# Revit family: Geberit pisuvar Preda, entegre deşarj kontrollü, elektrikli_PRO_224443
name_source: partatom
category: Plumbing Fixtures
revit_build: Autodesk Revit 2018 (Build: 20190510_1515(x64)
units: mm (PartAtom-declared; Revit-internal decimal feet)

## family parameters
Always vertical = Yes
Cut with Voids When Loaded = No
OmniClass Number = 23.45.05.21
OmniClass Title = Plumbing Fixtures - Sanitary Disposal Units
Part Type = Normal
Room Calculation Point = Yes
Round Connector Dimension = Use Diameter
Shared = No
Work Plane-Based = No

## types (1)
- 116.072.00.1 Geberit pisuvar Preda, entegre deşarj kontrollü, elektrikli
    116072_0_view = Yes
    Application purposes = Otomatik, su tasarrufu sağlayan deşarj ile kullanım için
Entegre kumandalı veya entegre kumandaya yönelik pisuvarlarda Geberit montaj elemanları için
    Application range = Plumbing fixture
    Article number key = 116.072.00.1
    BIM Content Version = GEB MG 1.2
    BIM Content revision date = 2020.05.18
    Bekleme modunda güç tüketimi = < 0.1 W
    Brand = Geberit
    CW Connection = Yes
    Characteristics = Bacak algılamalı IR kullanıcı algılaması
Kanalsız
Pisuvar deşarj kontrolü seramik çıkarılmadan önden değiştirilebilir
Püskürtme başlığı, seramik çıkarılmadan önden değiştirilebilir
Sifon, seramik çıkarılmadan yukarıdan değiştirilebilir
Sifon bağlantısının yüksekliği takımsız olarak ayarlanabilir
Drenaj sistemi seramik çıkarılmadan temizlenebilir
Su tasarrufu sağlayan hibrit modu ayarlanabilir
Anti-vandal
Ön deşarj ayarlanabilir
Güç kesintisi kontrolü
Elektrik kesildiğinde valf kapatma fonksiyonu
Geberit servis kumandası ile fonksiyonlar ayarlanabilir ve sorgulanabilir
Yıkama miktarı, deşarj süresi üzerinden deşarj başına 0,5 litreye kadar azaltılabilir
Pisuvar seramiği için deşarj başına 0,5 litre deşarj suyu garanti edilir, EN 13407 uyarınca
DIN 4109 uyarınca batarya grubu II
    Description = Geberit pisuvar Preda, entegre deşarj kontrollü, elektrikli
    EAN code basic data = 4025416529828
    GEB_culture = tr-TR
    GEB_generic_description = Bathroom collection
    GEB_generic_manufacturer = generic
    GEB_pimversion = 22.02.12
    GEB_processing_type = T
    GEB_reference = PRO_224443
    GEB_translations = {"ATT_10673":"EAN code basic data","ATT_10773":"Çalışma basıncı","ATT_10847":"Hesaplanan akış hızı için minimum akış basıncı","ATT_459792":"Renk / Yüzey","ATT_10851":"Nominal şebeke gerilimi","ATT_10853":"Şebeke frekansı","ATT_10817":"Güç tüketimi","ATT_156863":"Bekleme modunda güç tüketimi","applicationPurposes":"Application purposes","application_range":"Application range","brandName":"Brand","characteristics":"Characteristics","content_creator":"BIM Content creator","content_date_changed":"BIM Content revision date","content_version":"BIM Content Version","key 1000":"Article number key","name":"Name","productBrand":"Product brand","scopeOfDelivery":"Scope of delivery","type":"Type","ATT_10767":"Hesaplanan akış hızı","fixed_material":"Main material"}
    Güç tüketimi = < 0.5 W
    HW Connection = No
    Hesaplanan akış hızı = 0.2 L/s
    Hesaplanan akış hızı için minimum akış basıncı = 1 bar
    IfcDescription = Geberit pisuvar Preda, entegre deşarj kontrollü, elektrikli
    IfcExportAs = IfcSanitaryTerminal
    IfcExportType = URINAL
    LOD300 = No
    LOD400 = Yes
    Main material = Geberit, Plastic, Opaque white
    Manufacturer = Geberit
    Model = Preda (Preda)
    Name = Geberit pisuvar Preda, entegre deşarj kontrollü, elektrikli
    Nominal şebeke gerilimi = 110-240 V AC
    Renk / Yüzey = Beyaz
    Scope of delivery = Güç üniteli ve solenoid valfli pisuvar deşarj kontrolü
Sabitleme malzemesi
Emme fonksiyonlu pisuvar sifonu
Drenaj süzgeci
Tahliye ekipmanı
Giriş ekipmanı
Basınç düşürücü
    Type = Preda (Preda)
    Vent Connection = No
    Waste Connection = Yes
    outlet_flow = 0.0 L/s
    Çalışma basıncı = 1-8 bar
    Şebeke frekansı = 50-60 Hz

## geometry (parser evidence)
native form markers: Blend x8, Sweep x14
no freeform markers — native parametric forms only
